# Revit family: BOS-Dehnungsfugenzarge-BuHd1_Familie
name_source: partatom
category: Türen
revit_build: Autodesk Revit 2017 (Build: 20160225_1515(x64)
units: mm (PartAtom-declared; Revit-internal decimal feet)

## family parameters
Basisbauteil = Wand
Beim Laden mit Abzugskörper schneiden = Nein
Gemeinsam genutzt = Nein
Immer vertikal = Ja
Raumberechnungspunkt = Ja

## types (4) — shared parameters
Allgemeine Informationen zu Stahlzargen = www.BestOfSteel.de/tools-downloads/technische-infos-rund-um-die-stahlzarge/
BBL1 Bandbezugslinie   Hinge Position 1 = 241 mm  [stored 0.790682 ft]
BE max. = 100 mm  [stored 0.328084 ft]
Bauelement = BOS Stahlzarge
Blechstärke = 1.5 mm  [stored 0.00492126 ft]
Dehnungsfuge max. = 50 mm  [stored 0.164042 ft]
Dehnungsfuge min. = 10 mm  [stored 0.0328084 ft]
Dichtung 1 = Ja
Einfügepunkt = 30 mm  [stored 0.0984252 ft]
FMB max. = 1341 mm  [stored 4.39961 ft]
FMB min. = 591 mm  [stored 1.93898 ft]
FMH max. = 2858 mm  [stored 9.37664 ft]
FMH min. = 1608 mm  [stored 5.27559 ft]
Falzaufschlag = 15 mm  [stored 0.0492126 ft]
Falztiefe 2 = 25 mm  [stored 0.082021 ft]
Funktion = Innen
GT1 max. = 605 mm  [stored 1.98491 ft]
GT2 max. = 605 mm  [stored 1.98491 ft]
Hersteller = BOS GmbH Best Of Steel, Lütkenfelde 4, D-48282 Emsdetten
Info-Texte sichtbar = Ja
Information in English = Nein
MW1 min. = 130 mm  [stored 0.426509 ft]
MW2 min. = 100 mm  [stored 0.328084 ft]
Material = grundiert, feuerverzinktes Feinblech nach DIN EN 10143
Material - Bänder = <Nach Kategorie>
Material - Dichtung = <Nach Kategorie>
Material - Drückergarnitur = <Nach Kategorie>
Material - Türblatt = <Nach Kategorie>
Material - Zarge = <Nach Kategorie>
URL = www.BestOfSteel.de/stahlzargen/zargen-fuer-drehfluegeltueren/dehnungsfugenzargen/
zero-valued in all types: Breite, Dicke, Rohbaubreite, Rohbauhöhe

## per-type parameters (varying)
| type | Beschreibung | BsFHd1 | BsHd1 | BuFHd1 | BuHd1 | Dichtung 2 | Doppelfalz | Einfachfalz | Falzaufschlag gesamt | Falztiefe | Falztiefe gesamt | Gefälzt | Stumpf | Türblattstärke | Türblattstärke 1 | Türblattstärke 2 | Türblattstärke 3 |
| BuHd1 | Dehnungsfugenzarge Typ 1, nachträglicher Einbau, gefälzt | Nein | Nein | Nein | Ja | Nein | Nein | Ja | 15 mm  [stored 0.0492126 ft] | 28.5 mm  [stored 0.0935039 ft] | 28.5 mm  [stored 0.0935039 ft] | Ja | Nein | 40 mm  [stored 0.131234 ft] | 14.5 mm  [stored 0.0475722 ft] | 25.5 mm | 0 mm  [stored 0 ft] |
| BsHd1 | Dehnungsfugenzarge Typ 1, nachträglicher Einbau, stumpf | Nein | Ja | Nein | Nein | Nein | Nein | Ja | 15 mm  [stored 0.0492126 ft] | 46.5 mm  [stored 0.152559 ft] | 46.5 mm  [stored 0.152559 ft] | Nein | Ja | 40 mm  [stored 0.131234 ft] | 0 mm  [stored 0 ft] | 40 mm  [stored 0.131234 ft] | 0 mm  [stored 0 ft] |
| BuFHd1 | Dehnungsfugenzarge Typ 1, nachträglicher Einbau, gefälzt, mit Doppelfalz | Nein | Nein | Ja | Nein | Ja | Ja | Nein | 30 mm  [stored 0.0984252 ft] | 28.5 mm  [stored 0.0935039 ft] | 53.5 mm  [stored 0.175525 ft] | Ja | Nein | 65 mm  [stored 0.213255 ft] | 14.5 mm  [stored 0.0475722 ft] | 25.5 mm | 25 mm  [stored 0.082021 ft] |
| BsFHd1 | Dehnungsfugenzarge Typ 1, nachträglicher Einbau, stumpf, mit Doppelfalz | Ja | Nein | Nein | Nein | Ja | Ja | Nein | 30 mm  [stored 0.0984252 ft] | 46.5 mm  [stored 0.152559 ft] | 71.5 mm | Nein | Ja | 65 mm  [stored 0.213255 ft] | 0 mm  [stored 0 ft] | 40 mm  [stored 0.131234 ft] | 25 mm  [stored 0.082021 ft] |

note: column(s) folded — value = type name in every type: Modell

note: [stored X ft] marks values corroborated as IEEE doubles in the binary element streams (Revit-internal decimal feet)
